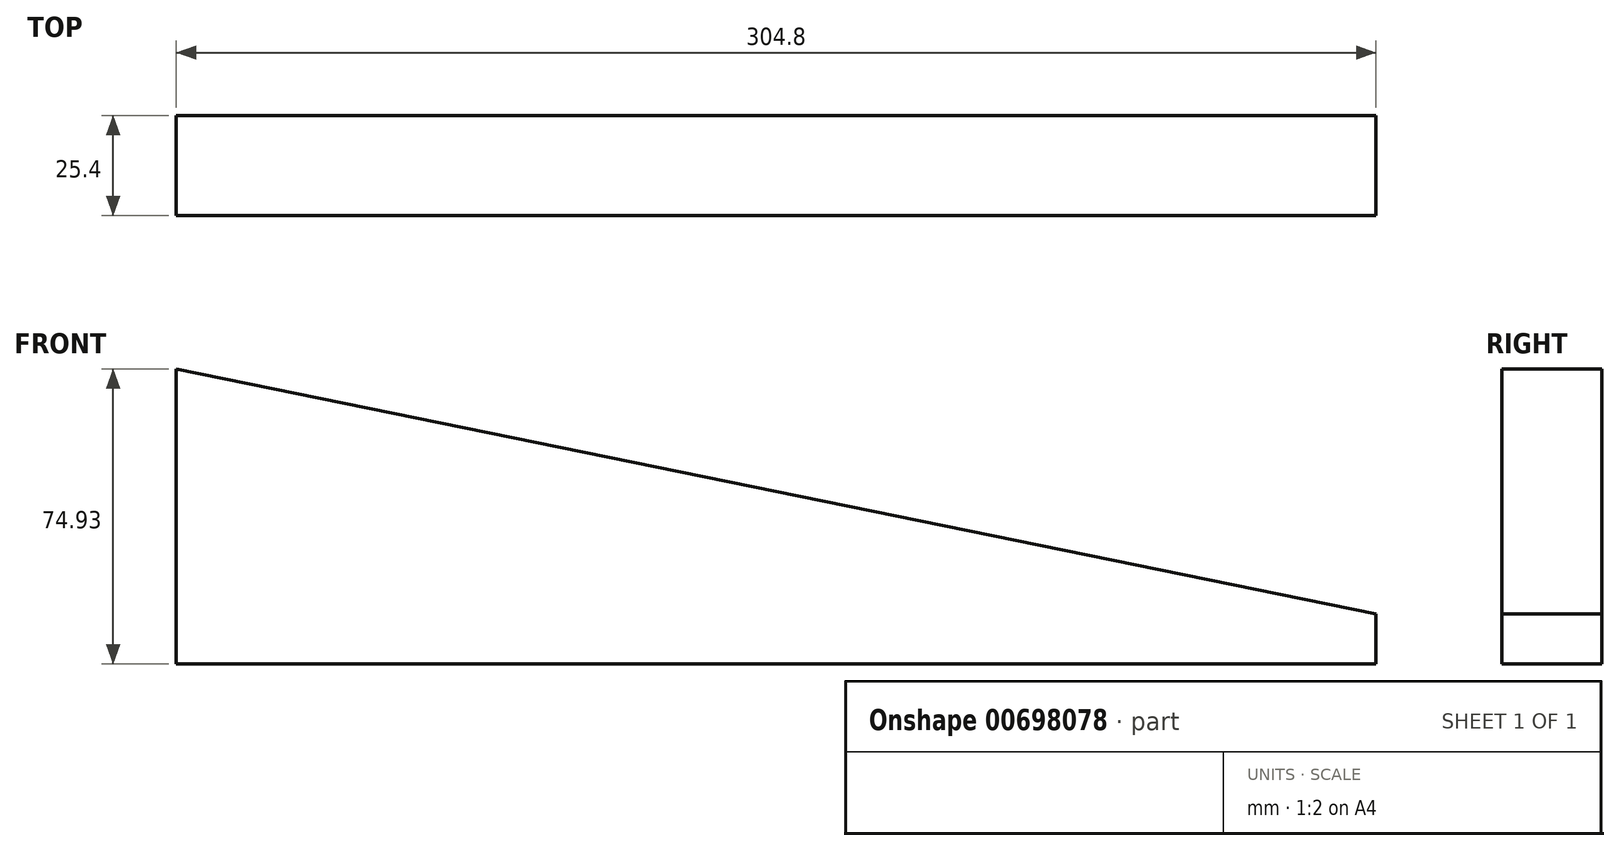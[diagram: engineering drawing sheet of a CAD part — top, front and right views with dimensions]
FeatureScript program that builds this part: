
annotation { "Feature Type Name" : "Feature", "Feature Type Description" : "" }
export const myFeature = defineFeature(function(context is Context, id is Id, definition is map)
    precondition{}
    {
        {
            var Q0;
            Q0=qCreatedBy(makeId("Front.planeOp"),FACE);
            var sketch = newSketch(context, id + "F0", { "sketchPlane" : qUnion([Q0])});
            skLineSegment(sketch, "E0", {"start": v(176.07, -80.47) * mm, "end": v(480.87, -80.47) * mm});
            skLineSegment(sketch, "E1", {"start": v(176.07, -80.47) * mm, "end": v(176.07, -5.54) * mm});
            skLineSegment(sketch, "E2", {"start": v(480.87, -80.47) * mm, "end": v(480.87, -67.77) * mm});
            skLineSegment(sketch, "E3", {"start": v(176.07, -5.54) * mm, "end": v(480.87, -67.77) * mm});
            skSolve(sketch);
        }
        {
            var Q0;
            Q0 = qSketchRegion(id + "F0", true);
            extrude(context, id + "F1", {"entities" : qUnion([Q0]), "depth" : 25.4 * mm, "offsetDistance" : 25.4 * mm});
        }
    });
